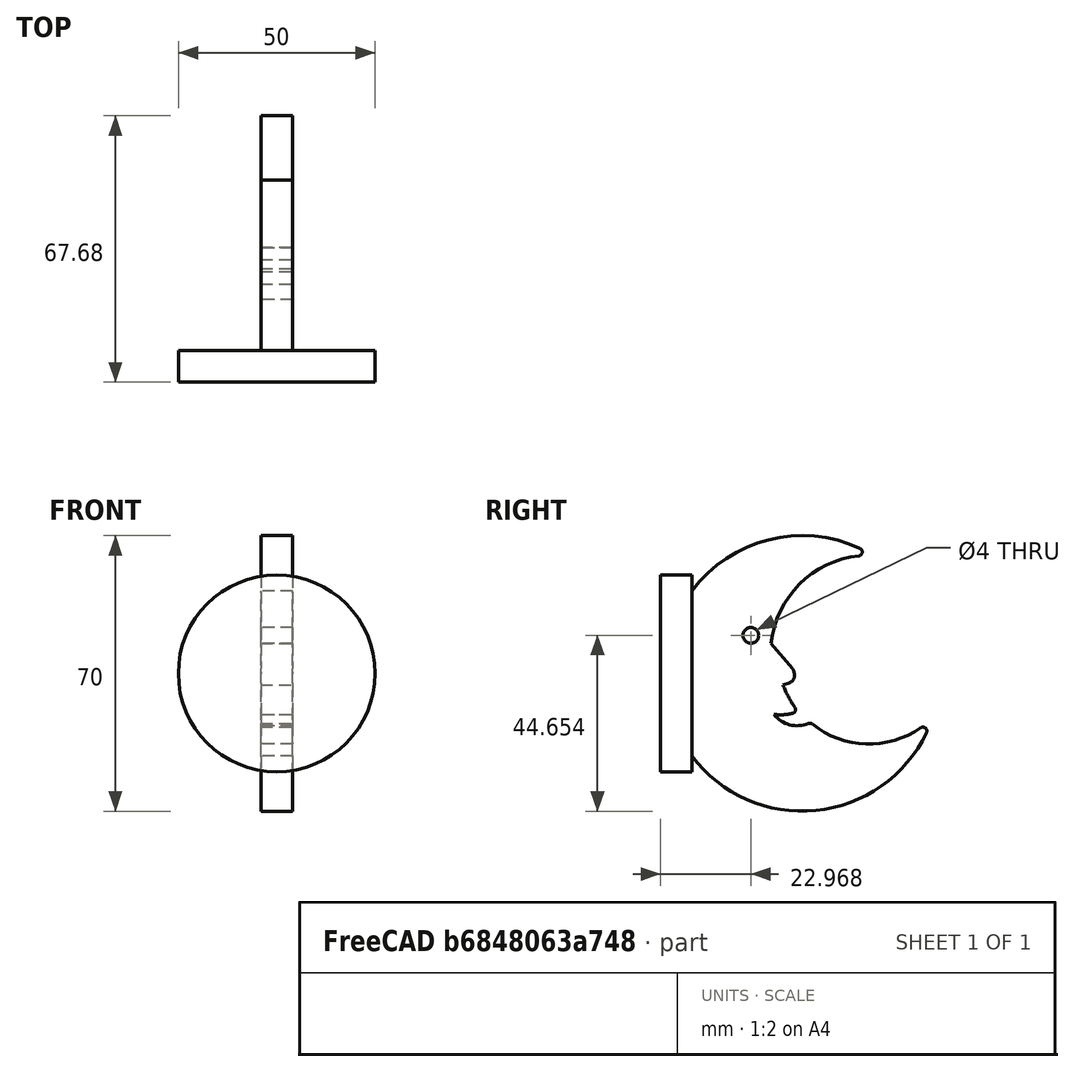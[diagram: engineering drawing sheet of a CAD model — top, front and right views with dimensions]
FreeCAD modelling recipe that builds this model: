
FCSTD DOCUMENT  (FreeCAD 0.18R16146 (Git))
Label: kleiderhaken_mond
License: All rights reserved
LicenseURL: http://en.wikipedia.org/wiki/All_rights_reserved
objects: Sketcher::SketchObject×3, PartDesign::Pad×2, PartDesign::Fillet×2, PartDesign::Body×1, Mesh::Feature×1
note: 10 computed .brp shape members not serialized (recipe doc carries the construction recipe); baked Part::Feature solids carry a one-line shape summary decoded from their .brp

FEATURE [Sketcher::SketchObject] Sketch
  MapMode = 5
  Placement = pos=(0,0,0) rot=(1,0,0;1.5708rad)
  Support = -> [XZ_Plane]
  sketch-geometry (1):
    g0: Circle CenterX=0 CenterY=0 CenterZ=0 NormalX=0 NormalY=0 NormalZ=1 AngleXU=0 Radius=25
  constraints (2):
    c: Coincident(g0,g-1)
    c: Diameter(g0) = 50
FEATURE [PartDesign::Pad] Pad
  Length = 8
  Length2 = 100
  Placement = pos=(0,0,0) rot=(1,0,0;1.5708rad)
  Profile = -> Sketch
  Refine = true
  Type = 0
FEATURE [Sketcher::SketchObject] Sketch001
  MapMode = 5
  Placement = pos=(0,0,0) rot=(0.57735,0.57735,0.57735;2.0944rad)
  Support = -> [YZ_Plane]
FEATURE [Sketcher::SketchObject] Sketch002
  MapMode = 5
  Placement = pos=(0,0,0) rot=(0.57735,0.57735,0.57735;2.0944rad)
  Support = -> [YZ_Plane]
  sketch-geometry (12):
    g0: ArcOfCircle CenterX=28 CenterY=0 CenterZ=0 NormalX=0 NormalY=0 NormalZ=1 AngleXU=0 Radius=35 StartAngle=1.02844 EndAngle=5.95346
    g1: ArcOfCircle CenterX=45 CenterY=5 CenterZ=0 NormalX=0 NormalY=0 NormalZ=1 AngleXU=0 Radius=25 StartAngle=1.52816 EndAngle=3.03827
    g2: Circle CenterX=14.9683 CenterY=9.65364 CenterZ=0 NormalX=0 NormalY=0 NormalZ=1 AngleXU=0 Radius=2
    g3: ArcOfCircle CenterX=22.4286 CenterY=2.50612 CenterZ=0 NormalX=0 NormalY=0 NormalZ=1 AngleXU=0 Radius=13.0302 StartAngle=4.58955 EndAngle=5.0706
    g4: ArcOfCircle CenterX=26.7339 CenterY=-5.79794 CenterZ=0 NormalX=0 NormalY=0 NormalZ=1 AngleXU=0 Radius=7.5 StartAngle=3.8066 EndAngle=5.18361
    g5: ArcOfCircle CenterX=45 CenterY=5 CenterZ=0 NormalX=0 NormalY=0 NormalZ=1 AngleXU=0 Radius=22.944 StartAngle=4.0078 EndAngle=5.49107
    g6: LineSegment StartX=20.1333 StartY=7.57858 StartZ=0 EndX=25.4735 EndY=1.29839 EndZ=0
    g7: LineSegment StartX=25.9319 StartY=0.342185 StartZ=0 EndX=26.033 EndY=-0.18504 EndZ=0
    g8: LineSegment StartX=24.7979 StartY=-2.36775 StartZ=0 EndX=23.1674 EndY=-2.96561 EndZ=0
    g9: ArcOfCircle CenterX=45 CenterY=5 CenterZ=0 NormalX=0 NormalY=0 NormalZ=1 AngleXU=0 Radius=23.2403 StartAngle=3.49144 EndAngle=3.82623
    g10: ArcOfCircle CenterX=24.1313 CenterY=-0.549735 CenterZ=0 NormalX=0 NormalY=0 NormalZ=1 AngleXU=0 Radius=1.93638 StartAngle=5.06384 EndAngle=6.47266
    g11: ArcOfCircle CenterX=23.888 CenterY=-0.0497864 CenterZ=0 NormalX=0 NormalY=0 NormalZ=1 AngleXU=0 Radius=2.0812 StartAngle=0.18947 EndAngle=0.704678
  constraints (21):
    c: PointOnObject(g0,g-1)
    c: Coincident(g1,g0)
    c: Coincident(g5,g0)
    c: Diameter(g0) = 70
    c: DistanceX(g0) = 28
    c: Diameter(g1) = 50
    c: DistanceY(g1) = 5
    c: DistanceX(g1) = 45
    c: Coincident(g9,g3)
    c: Coincident(g5,g4)
    c: Coincident(g1,g5)
    c: Coincident(g1,g6)
    c: Coincident(g9,g8)
    c: Coincident(g1,g9)
    c: Tangent(g7,g10) = 1.5708
    c: Tangent(g8,g10) = 1.5708
    c: Tangent(g6,g11) = 1.5708
    c: Tangent(g7,g11) = 1.5708
    c: Diameter(g2) = 4
    c: Coincident(g3,g4)
    c: Diameter(g4) = 15
FEATURE [PartDesign::Pad] Pad001
  BaseFeature = -> Pad
  Length = 8
  Length2 = 100
  Midplane = true
  Placement = pos=(0,0,0) rot=(1,0,0;1.5708rad)
  Profile = -> Sketch002
  Refine = true
  Type = 0
FEATURE [PartDesign::Fillet] Fillet
  Base = -> Pad001 [Edge22,Edge35]
  BaseFeature = -> Pad001
  Placement = pos=(0,0,0) rot=(1,0,0;1.5708rad)
  Radius = 1
FEATURE [PartDesign::Fillet] Fillet001
  Base = -> Fillet [Edge43,Edge42]
  BaseFeature = -> Fillet
  Placement = pos=(0,0,0) rot=(1,0,0;1.5708rad)
  Radius = 1
FEATURE [PartDesign::Body] Body
  Group = -> [Sketch,Pad,Sketch001,Sketch002,Pad001,Fillet,Fillet001]
  Origin = -> Origin
  Tip = -> Fillet001
FEATURE [Mesh::Feature] Mesh  label="Fillet001 (Meshed)"
